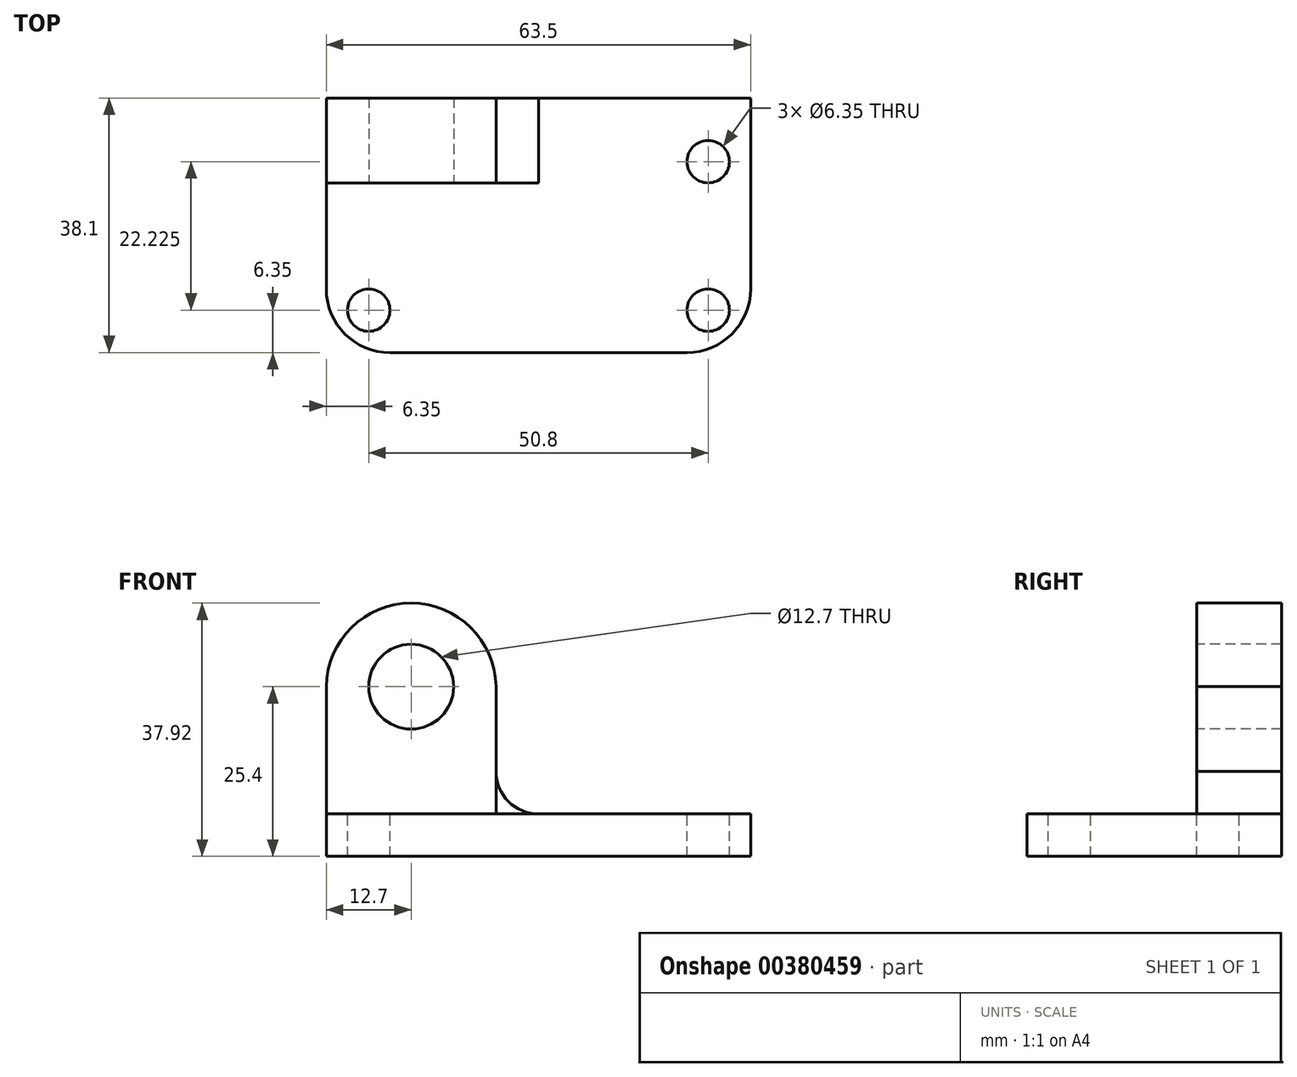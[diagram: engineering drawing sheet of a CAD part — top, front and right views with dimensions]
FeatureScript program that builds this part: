
annotation { "Feature Type Name" : "Feature", "Feature Type Description" : "" }
export const myFeature = defineFeature(function(context is Context, id is Id, definition is map)
    precondition{}
    {
        {
            var Q0;
            Q0=qCreatedBy(makeId("Top.planeOp"),FACE);
            var sketch = newSketch(context, id + "F0", { "sketchPlane" : qUnion([Q0])});
            skLineSegment(sketch, "E0", {"start": v(0, 0) * mm, "end": v(63.5, 0) * mm});
            skLineSegment(sketch, "E1", {"start": v(63.5, 0) * mm, "end": v(63.5, 38.1) * mm});
            skLineSegment(sketch, "E2", {"start": v(63.5, 38.1) * mm, "end": v(0, 38.1) * mm});
            skLineSegment(sketch, "E3", {"start": v(0, 38.1) * mm, "end": v(0, 0) * mm});
            skSolve(sketch);
        }
        {
            var Q0;
            Q0 = qSketchRegion(id + "F0", true);
            extrude(context, id + "F1", {"entities" : qUnion([Q0]), "depth" : 6.35 * mm});
        }
        {
            var Q0;
            Q0=makeQuery(id+"F1.opExtrude","CAP_FACE",FACE,{"disambiguationData":[OSD([sQuery(id+"F0.wireOp",EDGE,"E0"),sQuery(id+"F0.wireOp",EDGE,"E1"),sQuery(id+"F0.wireOp",EDGE,"E2"),sQuery(id+"F0.wireOp",EDGE,"E3")])],"isStart":false});
            var sketch = newSketch(context, id + "F2", { "sketchPlane" : qUnion([Q0])});
            skCircle(sketch, "E4", {"center": v(6.35, 6.35) * mm, "radius": 3.18 * mm});
            skCircle(sketch, "E5", {"center": v(57.15, 6.35) * mm, "radius": 3.18 * mm});
            skCircle(sketch, "E6", {"center": v(57.15, 28.58) * mm, "radius": 3.18 * mm});
            skSolve(sketch);
        }
        {
            var Q0;
            Q0=makeQuery(id+"F2.imprint","IMPRINT",FACE,{"disambiguationData":[TD([[makeQuery(id+"F2.imprint","IMPRINT",EDGE,{"derivedFrom":sQuery(id+"F2.wireOp",EDGE,"E4")}),1.0]])]});
            var Q1;
            Q1=makeQuery(id+"F2.imprint","IMPRINT",FACE,{"disambiguationData":[TD([[makeQuery(id+"F2.imprint","IMPRINT",EDGE,{"derivedFrom":sQuery(id+"F2.wireOp",EDGE,"E5")}),1.0]])]});
            var Q2;
            Q2=makeQuery(id+"F2.imprint","IMPRINT",FACE,{"disambiguationData":[TD([[makeQuery(id+"F2.imprint","IMPRINT",EDGE,{"derivedFrom":sQuery(id+"F2.wireOp",EDGE,"E6")}),1.0]])]});
            extrude(context, id + "F3", {"entities" : qUnion([Q0, Q1, Q2]), "operationType" : NewBodyOperationType.REMOVE, "oppositeDirection" : true, "depth" : 25.4 * mm});
        }
        {
            var Q0;
            Q0=makeQuery(id+"F1.opExtrude","CAP_FACE",FACE,{"disambiguationData":[OSD([sQuery(id+"F0.wireOp",EDGE,"E0"),sQuery(id+"F0.wireOp",EDGE,"E1"),sQuery(id+"F0.wireOp",EDGE,"E2"),sQuery(id+"F0.wireOp",EDGE,"E3")])],"isStart":false});
            var sketch = newSketch(context, id + "F4", { "sketchPlane" : qUnion([Q0])});
            skLineSegment(sketch, "E7", {"start": v(0, 25.4) * mm, "end": v(25.4, 25.4) * mm});
            skLineSegment(sketch, "E8", {"start": v(25.4, 25.4) * mm, "end": v(25.4, 38.1) * mm});
            skSolve(sketch);
        }
        {
            var Q0;
            Q0 = qSketchRegion(id + "F4", true);
            var Q1;
            {var subQ0=sQuery(id+"F4.wireOp",EDGE,"E7");Q1=makeQuery(id+"F4.imprint","IMPRINT",FACE,{"disambiguationData":[TD([[makeQuery(id+"F4.imprint","IMPRINT",EDGE,{"derivedFrom":subQ0}),1.0]])]});}
            extrude(context, id + "F5", {"entities" : qUnion([Q0, Q1]), "operationType" : NewBodyOperationType.ADD, "depth" : 31.75 * mm, "offsetDistance" : 25.4 * mm});
        }
        {
            var Q0;
            Q0=makeQuery(id+"F5.opExtrude","SWEPT_FACE",FACE,{"disambiguationData":[OSD([sQuery(id+"F4.wireOp",EDGE,"E7")])]});
            var sketch = newSketch(context, id + "F6", { "sketchPlane" : qUnion([Q0])});
            skCircle(sketch, "E9", {"center": v(12.7, 25.4) * mm, "radius": 6.35 * mm});
            skArc(sketch, "E10", {"start": v(25.4, 25.4) * mm, "mid": v(12.7, 37.92) * mm, "end": v(0, 25.4) * mm});
            skSolve(sketch);
        }
        {
            var Q0;
            Q0 = qSketchRegion(id + "F6", true);
            var Q1;
            {var subQ0=sQuery(id+"F6.wireOp",EDGE,"E10");Q1=makeQuery(id+"F6.imprint","IMPRINT",FACE,{"disambiguationData":[TD([[makeQuery(id+"F6.imprint","IMPRINT",EDGE,{"derivedFrom":subQ0}),-1.0]])]});}
            extrude(context, id + "F7", {"entities" : qUnion([Q0, Q1]), "operationType" : NewBodyOperationType.REMOVE, "oppositeDirection" : true, "depth" : 25.4 * mm});
        }
        {
            var Q0;
            Q0=makeQuery(id+"F5.opExtrude","SWEPT_FACE",FACE,{"disambiguationData":[OSD([sQuery(id+"F4.wireOp",EDGE,"E7")])]});
            var sketch = newSketch(context, id + "F8", { "sketchPlane" : qUnion([Q0])});
            skCircle(sketch, "E11", {"center": v(31.75, 12.7) * mm, "radius": 6.35 * mm});
            skLineSegment(sketch, "E12", {"start": v(25.4, 19.05) * mm, "end": v(38.1, 19.05) * mm});
            skLineSegment(sketch, "E13", {"start": v(38.1, 19.05) * mm, "end": v(38.1, 6.35) * mm});
            skLineSegment(sketch, "E14", {"start": v(38.1, 6.35) * mm, "end": v(25.4, 6.35) * mm});
            skLineSegment(sketch, "E15", {"start": v(25.4, 6.35) * mm, "end": v(25.4, 19.05) * mm});
            skSolve(sketch);
        }
        {
            var Q0;
            {var subQ0=sQuery(id+"F8.wireOp",EDGE,"E14");var subQ1=sQuery(id+"F8.wireOp",EDGE,"E11");var subQ2=makeQuery(id+"F8.imprint","INTERSECT",VERTEX,{"derivedFrom":[subQ1,subQ0]});Q0=makeQuery(id+"F8.imprint","IMPRINT",FACE,{"disambiguationData":[TD([[makeQuery(id+"F8.imprint","IMPRINT",EDGE,{"disambiguationData":[TD([[subQ2,1.0]])],"derivedFrom":subQ1}),-1.0]])]});}
            extrude(context, id + "F9", {"entities" : qUnion([Q0]), "oppositeDirection" : true, "depth" : 12.7 * mm});
        }
        {
            var Q0;
            Q0=makeQuery(id+"F1.opExtrude","SWEPT_EDGE",EDGE,{"disambiguationData":[OSD([sQuery(id+"F0.wireOp",EDGE,"E0"),sQuery(id+"F0.wireOp",EDGE,"E1")])]});
            var Q1;
            Q1=makeQuery(id+"F1.opExtrude","SWEPT_EDGE",EDGE,{"disambiguationData":[OSD([sQuery(id+"F0.wireOp",EDGE,"E0"),sQuery(id+"F0.wireOp",EDGE,"E3")])]});
            fillet(context, id + "F10", {"entities" : qUnion([Q0, Q1]), "radius" : 9.52 * mm, "tangentPropagation" : true, "allowEdgeOverflow" : false});
        }
    });
